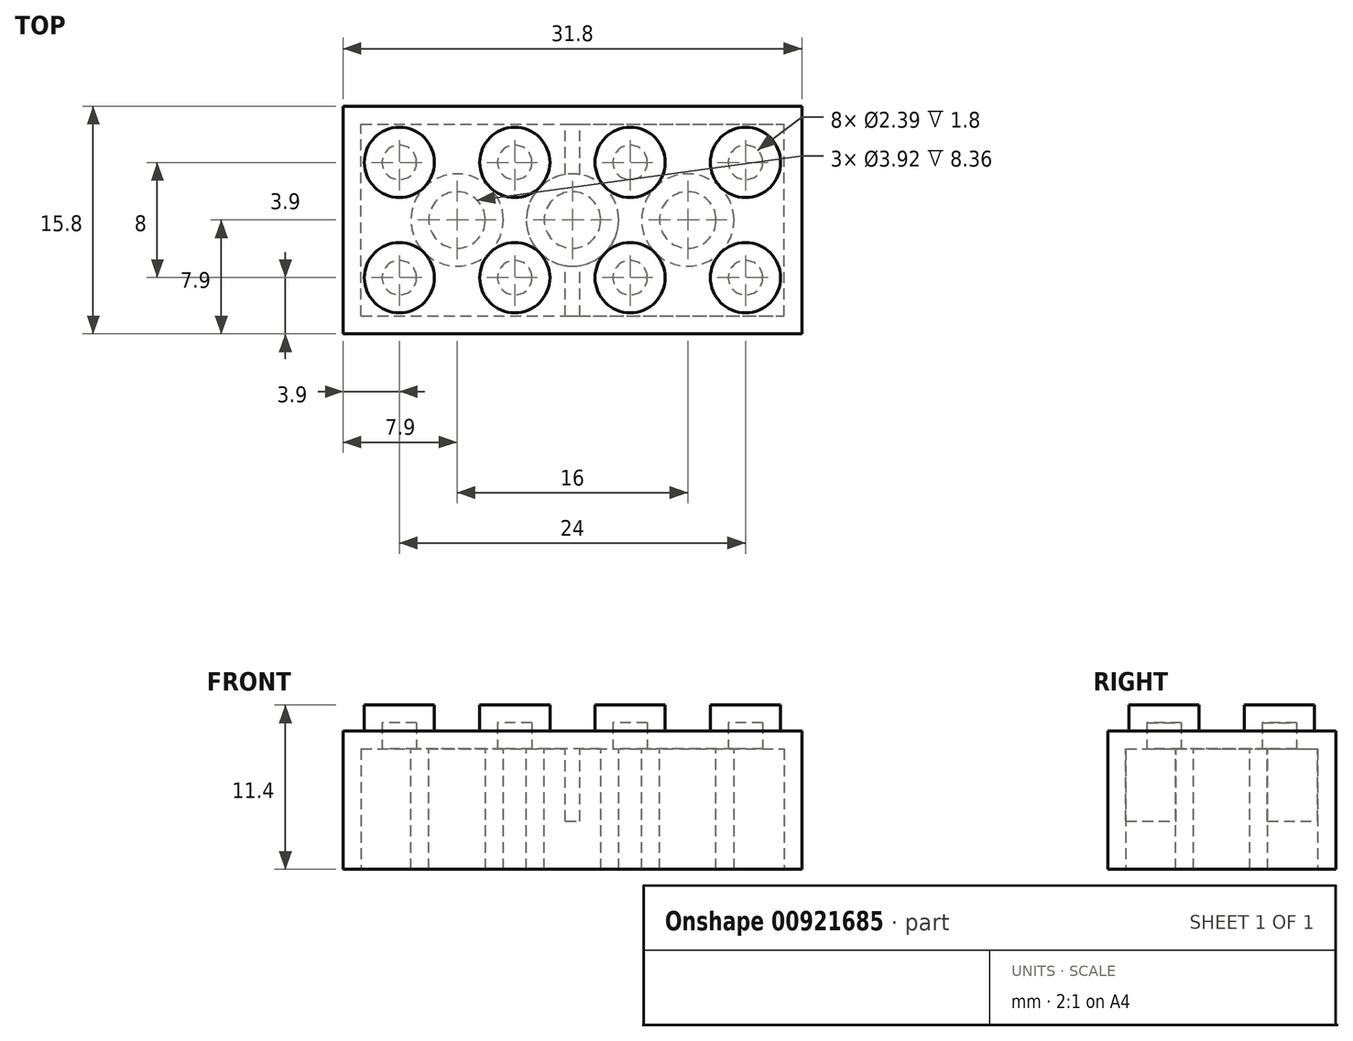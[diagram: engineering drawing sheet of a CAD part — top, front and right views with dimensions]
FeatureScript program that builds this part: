
annotation { "Feature Type Name" : "Feature", "Feature Type Description" : "" }
export const myFeature = defineFeature(function(context is Context, id is Id, definition is map)
    precondition{}
    {
        {
            var Q0;
            Q0=qCreatedBy(makeId("Top.planeOp"),FACE);
            var sketch = newSketch(context, id + "F0", { "sketchPlane" : qUnion([Q0])});
            skLineSegment(sketch, "E0.bottom", {"start": v(0, 0) * mm, "end": v(31.8, 0) * mm});
            skLineSegment(sketch, "E0.top", {"start": v(0, 15.8) * mm, "end": v(31.8, 15.8) * mm});
            skLineSegment(sketch, "E0.left", {"start": v(0, 0) * mm, "end": v(0, 15.8) * mm});
            skLineSegment(sketch, "E0.right", {"start": v(31.8, 0) * mm, "end": v(31.8, 15.8) * mm});
            skSolve(sketch);
        }
        {
            var Q0;
            Q0=makeQuery(id+"F0.imprint","IMPRINT",FACE,{"disambiguationData":[TD([[makeQuery(id+"F0.imprint","IMPRINT",EDGE,{"derivedFrom":sQuery(id+"F0.wireOp",EDGE,"E0.bottom")}),1.0]])]});
            extrude(context, id + "F1", {"entities" : qUnion([Q0]), "depth" : 9.6 * mm, "offsetDistance" : 25 * mm});
        }
        {
            var Q0;
            Q0=makeQuery(id+"F1.opExtrude","CAP_FACE",FACE,{"disambiguationData":[OSD([sQuery(id+"F0.wireOp",EDGE,"E0.bottom"),sQuery(id+"F0.wireOp",EDGE,"E0.top"),sQuery(id+"F0.wireOp",EDGE,"E0.left"),sQuery(id+"F0.wireOp",EDGE,"E0.right")])],"isStart":false});
            var sketch = newSketch(context, id + "F2", { "sketchPlane" : qUnion([Q0])});
            skLineSegment(sketch, "E1", {"start": v(0, 11.9) * mm, "end": v(31.8, 11.9) * mm, "construction": true});
            skLineSegment(sketch, "E2", {"start": v(0, 3.9) * mm, "end": v(31.8, 3.9) * mm, "construction": true});
            skLineSegment(sketch, "E3", {"start": v(3.9, 15.8) * mm, "end": v(3.9, 0) * mm, "construction": true});
            skLineSegment(sketch, "E4", {"start": v(15.9, 15.8) * mm, "end": v(15.9, 0) * mm, "construction": true});
            skLineSegment(sketch, "E5", {"start": v(27.9, 15.8) * mm, "end": v(27.9, 0) * mm, "construction": true});
            skLineSegment(sketch, "E6", {"start": v(11.9, 15.8) * mm, "end": v(11.9, 0) * mm, "construction": true});
            skLineSegment(sketch, "E7", {"start": v(19.9, 15.8) * mm, "end": v(19.9, 0) * mm, "construction": true});
            skCircle(sketch, "E8", {"center": v(3.9, 11.9) * mm, "radius": 2.44 * mm});
            skCircle(sketch, "E9", {"center": v(11.9, 11.9) * mm, "radius": 2.44 * mm});
            skCircle(sketch, "E10", {"center": v(19.9, 11.9) * mm, "radius": 2.44 * mm});
            skCircle(sketch, "E11", {"center": v(27.9, 11.9) * mm, "radius": 2.44 * mm});
            skCircle(sketch, "E12", {"center": v(27.9, 3.9) * mm, "radius": 2.44 * mm});
            skCircle(sketch, "E13", {"center": v(19.9, 3.9) * mm, "radius": 2.44 * mm});
            skCircle(sketch, "E14", {"center": v(11.9, 3.9) * mm, "radius": 2.44 * mm});
            skCircle(sketch, "E15", {"center": v(3.9, 3.9) * mm, "radius": 2.44 * mm});
            skSolve(sketch);
        }
        {
            var Q0;
            Q0=makeQuery(id+"F2.imprint","IMPRINT",FACE,{"disambiguationData":[TD([[makeQuery(id+"F2.imprint","IMPRINT",EDGE,{"derivedFrom":sQuery(id+"F2.wireOp",EDGE,"E9")}),1.0]])]});
            var Q1;
            Q1=makeQuery(id+"F2.imprint","IMPRINT",FACE,{"disambiguationData":[TD([[makeQuery(id+"F2.imprint","IMPRINT",EDGE,{"derivedFrom":sQuery(id+"F2.wireOp",EDGE,"E10")}),1.0]])]});
            var Q2;
            Q2=makeQuery(id+"F2.imprint","IMPRINT",FACE,{"disambiguationData":[TD([[makeQuery(id+"F2.imprint","IMPRINT",EDGE,{"derivedFrom":sQuery(id+"F2.wireOp",EDGE,"E11")}),1.0]])]});
            var Q3;
            Q3=makeQuery(id+"F2.imprint","IMPRINT",FACE,{"disambiguationData":[TD([[makeQuery(id+"F2.imprint","IMPRINT",EDGE,{"derivedFrom":sQuery(id+"F2.wireOp",EDGE,"E12")}),1.0]])]});
            var Q4;
            Q4=makeQuery(id+"F2.imprint","IMPRINT",FACE,{"disambiguationData":[TD([[makeQuery(id+"F2.imprint","IMPRINT",EDGE,{"derivedFrom":sQuery(id+"F2.wireOp",EDGE,"E13")}),1.0]])]});
            var Q5;
            Q5=makeQuery(id+"F2.imprint","IMPRINT",FACE,{"disambiguationData":[TD([[makeQuery(id+"F2.imprint","IMPRINT",EDGE,{"derivedFrom":sQuery(id+"F2.wireOp",EDGE,"E14")}),1.0]])]});
            var Q6;
            Q6=makeQuery(id+"F2.imprint","IMPRINT",FACE,{"disambiguationData":[TD([[makeQuery(id+"F2.imprint","IMPRINT",EDGE,{"derivedFrom":sQuery(id+"F2.wireOp",EDGE,"E15")}),1.0]])]});
            var Q7;
            Q7=makeQuery(id+"F2.imprint","IMPRINT",FACE,{"disambiguationData":[TD([[makeQuery(id+"F2.imprint","IMPRINT",EDGE,{"derivedFrom":sQuery(id+"F2.wireOp",EDGE,"E8")}),1.0]])]});
            extrude(context, id + "F3", {"entities" : qUnion([Q0, Q1, Q2, Q3, Q4, Q5, Q6, Q7]), "operationType" : NewBodyOperationType.ADD, "depth" : 1.8 * mm, "offsetDistance" : 25 * mm});
        }
        {
            var Q0;
            Q0=makeQuery(id+"F1.opExtrude","CAP_FACE",FACE,{"disambiguationData":[OSD([sQuery(id+"F0.wireOp",EDGE,"E0.bottom"),sQuery(id+"F0.wireOp",EDGE,"E0.top"),sQuery(id+"F0.wireOp",EDGE,"E0.left"),sQuery(id+"F0.wireOp",EDGE,"E0.right")])],"isStart":true});
            shell(context, id + "F4", {"entities" : qUnion([Q0]), "thickness" : 1.24 * mm});
        }
        {
            var Q0;
            Q0=makeQuery(id+"F4.opShell","OFFSET_FACE",FACE,{"disambiguationData":[OSD([sQuery(id+"F0.wireOp",EDGE,"E0.bottom"),sQuery(id+"F0.wireOp",EDGE,"E0.top"),sQuery(id+"F0.wireOp",EDGE,"E0.left"),sQuery(id+"F0.wireOp",EDGE,"E0.right")])]});
            var sketch = newSketch(context, id + "F5", { "sketchPlane" : qUnion([Q0])});
            skLineSegment(sketch, "E16", {"start": v(1.24, -7.9) * mm, "end": v(30.56, -7.9) * mm, "construction": true});
            skLineSegment(sketch, "E17", {"start": v(15.9, -1.24) * mm, "end": v(15.9, -14.56) * mm, "construction": true});
            skLineSegment(sketch, "E18", {"start": v(7.9, -1.24) * mm, "end": v(7.9, -14.56) * mm, "construction": true});
            skLineSegment(sketch, "E19", {"start": v(23.9, -1.24) * mm, "end": v(23.9, -14.56) * mm, "construction": true});
            skLineSegment(sketch, "E20", {"start": v(4.7, -1.24) * mm, "end": v(4.7, -14.56) * mm, "construction": true});
            skLineSegment(sketch, "E21", {"start": v(27.1, -1.24) * mm, "end": v(27.1, -14.56) * mm, "construction": true});
            skLineSegment(sketch, "E22", {"start": v(1.24, -4.7) * mm, "end": v(30.56, -4.7) * mm, "construction": true});
            skCircle(sketch, "E23", {"center": v(7.9, -7.9) * mm, "radius": 3.2 * mm});
            skCircle(sketch, "E24", {"center": v(15.9, -7.9) * mm, "radius": 3.2 * mm});
            skCircle(sketch, "E25", {"center": v(23.9, -7.9) * mm, "radius": 3.2 * mm});
            skSolve(sketch);
        }
        {
            var Q0;
            Q0 = qSketchRegion(id + "F5", true);
            var Q1;
            Q1=makeQuery(id+"F1.opExtrude","CAP_FACE",FACE,{"disambiguationData":[OSD([sQuery(id+"F0.wireOp",EDGE,"E0.bottom"),sQuery(id+"F0.wireOp",EDGE,"E0.top"),sQuery(id+"F0.wireOp",EDGE,"E0.left"),sQuery(id+"F0.wireOp",EDGE,"E0.right")])],"isStart":true});
            var Q2;
            {var subQ0=sQuery(id+"F0.wireOp",EDGE,"E0.left");var subQ1=sQuery(id+"F0.wireOp",EDGE,"E0.top");Q2=makeQuery(id+"F4.opShell","OFFSET_VERTEX",VERTEX,{"disambiguationData":[OSD([subQ1,subQ0]),TDD([makeQuery(id+"F1.opExtrude","CAP_VERTEX",VERTEX,{"disambiguationData":[OSD([subQ1,subQ0])],"isStart":true})])]});}
            extrude(context, id + "F6", {"entities" : qUnion([Q0]), "operationType" : NewBodyOperationType.ADD, "endBound" : BoundingType.UP_TO_SURFACE, "depth" : 25 * mm, "endBoundEntityFace" : qUnion([Q1]), "endBoundEntityVertex" : qUnion([Q2]), "offsetDistance" : 25 * mm});
        }
        {
            var Q0;
            Q0=makeQuery(id+"F6.opExtrude","CAP_FACE",FACE,{"disambiguationData":[OSD([sQuery(id+"F5.wireOp",EDGE,"E23")])],"isStart":false});
            var Q1;
            Q1=makeQuery(id+"F6.opExtrude","CAP_FACE",FACE,{"disambiguationData":[OSD([sQuery(id+"F5.wireOp",EDGE,"E24")])],"isStart":false});
            var Q2;
            Q2=makeQuery(id+"F6.opExtrude","CAP_FACE",FACE,{"disambiguationData":[OSD([sQuery(id+"F5.wireOp",EDGE,"E25")])],"isStart":false});
            shell(context, id + "F7", {"entities" : qUnion([Q0, Q1, Q2]), "thickness" : 1.24 * mm});
        }
        {
            var Q0;
            Q0=makeQuery(id+"F4.opShell","OFFSET_FACE",FACE,{"disambiguationData":[OSD([sQuery(id+"F0.wireOp",EDGE,"E0.bottom"),sQuery(id+"F0.wireOp",EDGE,"E0.top"),sQuery(id+"F0.wireOp",EDGE,"E0.left"),sQuery(id+"F0.wireOp",EDGE,"E0.right")])]});
            var sketch = newSketch(context, id + "F8", { "sketchPlane" : qUnion([Q0])});
            skLineSegment(sketch, "E26", {"start": v(15.9, -1.24) * mm, "end": v(15.9, -14.56) * mm, "construction": true});
            skLineSegment(sketch, "E27", {"start": v(15.4, -1.24) * mm, "end": v(15.4, -4.74) * mm});
            skLineSegment(sketch, "E28", {"start": v(16.4, -1.24) * mm, "end": v(16.4, -4.74) * mm});
            skLineSegment(sketch, "E29", {"start": v(15.4, -11.06) * mm, "end": v(15.4, -14.56) * mm});
            skLineSegment(sketch, "E30", {"start": v(16.4, -11.06) * mm, "end": v(16.4, -14.56) * mm});
            skArc(sketch, "E31", {"start": v(15.4, -11.06) * mm, "mid": v(15.9, -11.1) * mm, "end": v(16.4, -11.06) * mm});
            skArc(sketch, "E32.trimOffspring", {"start": v(16.4, -4.74) * mm, "mid": v(15.9, -4.7) * mm, "end": v(15.4, -4.74) * mm});
            skLineSegment(sketch, "E33", {"start": v(15.4, -1.24) * mm, "end": v(16.4, -1.24) * mm});
            skLineSegment(sketch, "E34", {"start": v(15.4, -14.56) * mm, "end": v(16.4, -14.56) * mm});
            skSolve(sketch);
        }
        {
            var Q0;
            Q0=makeQuery(id+"F8.imprint","IMPRINT",FACE,{"disambiguationData":[TD([[makeQuery(id+"F8.imprint","IMPRINT",EDGE,{"derivedFrom":sQuery(id+"F8.wireOp",EDGE,"E27")}),1.0]])]});
            var Q1;
            Q1=makeQuery(id+"F8.imprint","IMPRINT",FACE,{"disambiguationData":[TD([[makeQuery(id+"F8.imprint","IMPRINT",EDGE,{"derivedFrom":sQuery(id+"F8.wireOp",EDGE,"E29")}),1.0]])]});
            extrude(context, id + "F9", {"entities" : qUnion([Q0, Q1]), "operationType" : NewBodyOperationType.ADD, "depth" : 5 * mm, "offsetDistance" : 25 * mm});
        }
    });
